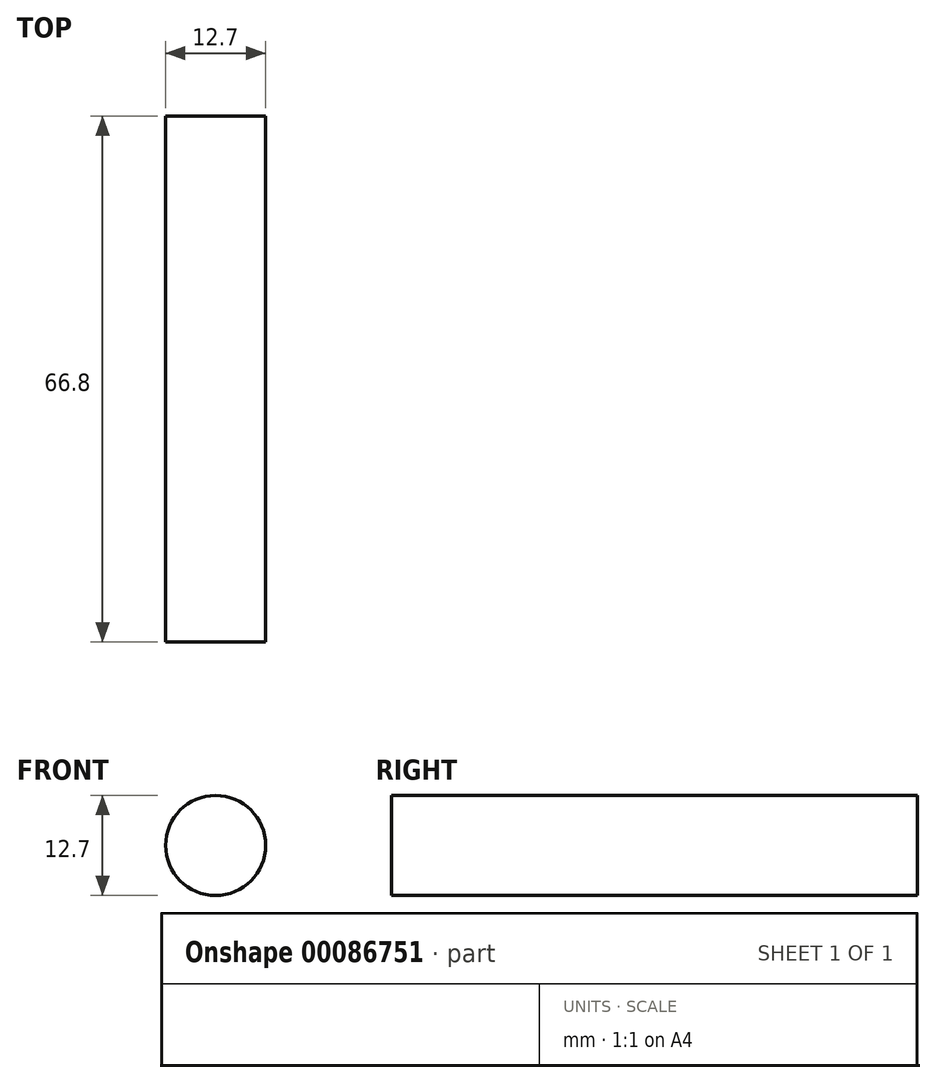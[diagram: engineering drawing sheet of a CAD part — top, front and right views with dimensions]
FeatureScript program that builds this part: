
annotation { "Feature Type Name" : "Feature", "Feature Type Description" : "" }
export const myFeature = defineFeature(function(context is Context, id is Id, definition is map)
    precondition{}
    {
        {
            var Q0;
            Q0=qCreatedBy(makeId("Front.planeOp"),FACE);
            var sketch = newSketch(context, id + "F0", { "sketchPlane" : qUnion([Q0])});
            skCircle(sketch, "E0", {"center": v(-17.47, 1.68) * mm, "radius": 6.35 * mm});
            skSolve(sketch);
        }
        {
            var Q0;
            Q0 = qSketchRegion(id + "F0", true);
            extrude(context, id + "F1", {"entities" : qUnion([Q0]), "depth" : 66.8 * mm});
        }
    });
